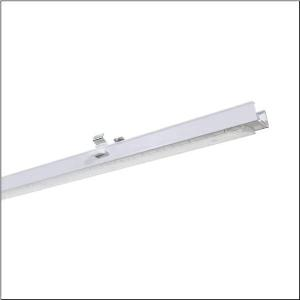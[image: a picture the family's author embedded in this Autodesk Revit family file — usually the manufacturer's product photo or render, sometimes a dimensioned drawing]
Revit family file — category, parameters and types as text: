
# Revit family: trunking_flex_31_51re18mb1cb
name_source: partatom
category: Lighting Fixtures
units: mm (PartAtom-declared; Revit-internal decimal feet)

## family parameters
Cut with Voids When Loaded = No
Host = Face
Light Source = No
Part Type = Normal
Room Calculation Point = No
Round Connector Dimension = Use Diameter
Shared = No

## types (1)
- --- (1 x LED, 11500 lm, 66 W, 3500K)
    Apparent Load = 66 VA
    CIE Flux Codes = 71 89 97 97 100
    Color Rendering = 80
    Color Temperature = 3500K
    Default Elevation = 1800 mm
    Description = Trunking Flex 31, luminaire insert, of extruded aluminium section, coated, traffic white (RAL 9016), length: 1.472mm, width: 91mm, height: 53mm, LED rated luminous flux: 11.500lm, light colour: 835, control gear: ON/OFF Multilumen, with system connector: socket, mains connection: 220..240V, AC, 50/60Hz, rated input power: 66W, luminous flux adjustable on luminaire in eight steps (3450/4380/5800/6700/8350/9200/10500/11500lm ), connected load according to luminous flux setting (19/24/32/37/47/52/60/66W), primary light control with lens, of plastic, primary optical cover: cover, of PMMA, light emission: direct distribution, protection rating (complete): IP20, insulation class (complete): insulation class I (protective earthing), certification: CE, UKCA, impact resistance: IK02, permissible ambient temperature for indoor applications: -20..+40°C, packaging unit: 1 piece
    Height = 58 mm
    Lamp = 1 x LED
    Lamp Light Flux = 11500 lm
    Lamp Power = 66 W
    Lamp count = 1
    Length = 1472 mm
    Luminous efficacy = 174 lm/W
    Manufacturer = Siteco
    ModVariant = No
    Model = 51RE18MB1CB
    Mounting Place = Ceiling
    Mounting Type = Pendant
    Number of Poles = 1
    OnlyDefault = Yes
    Power Factor = 1
    Product Name = Trunking Flex 31
    Product group = luminaire insert
    ProductGroupID = 901
    Protection Class = Protection class I
    Protection Degree = IP 20
    RLX_Detail_Level = 1
    RLX_Emergency_Light_Flux = 0 lm
    RLX_Emergency_Type = 0
    RLX_Emergency_Type_DB = No
    RlxData = <blob elided: 21157 chars, md5=360d91a8>
    Socket = socket
    Standby Power = 0 W
    System Light Flux = 11500 lm
    System Power = 66 W
    Type Comments = factory setting: luminous flux: 100 % | (ON | ON | ON)
    Type Image = l_1266702.jpg
    URL = http://relux.com
    VarID = @adj_018585
    Voltage = 0 V
    Weight = 0.00 kg
    Width = 65 mm

## geometry (parser evidence)
native form markers: Blend x4, Sweep x11
no freeform markers — native parametric forms only
